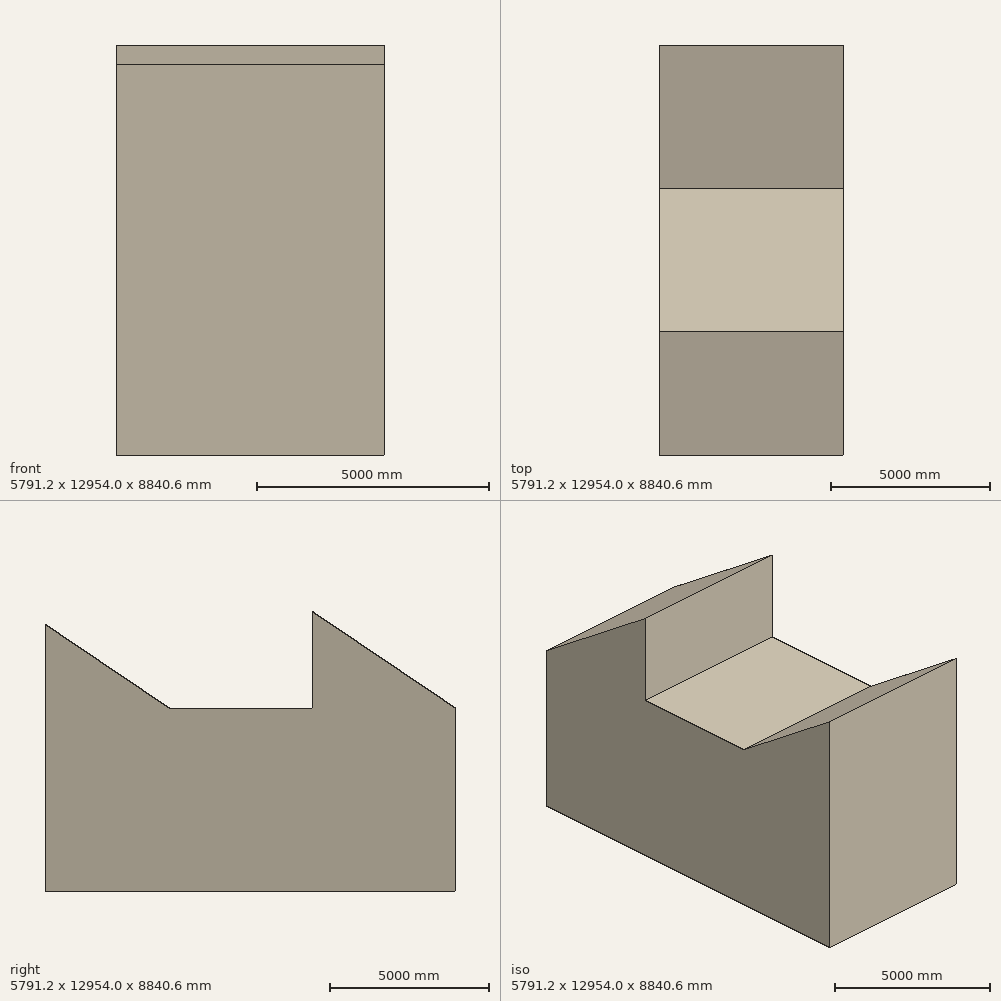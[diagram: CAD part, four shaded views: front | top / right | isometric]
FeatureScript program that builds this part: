
annotation { "Feature Type Name" : "Feature", "Feature Type Description" : "" }
export const myFeature = defineFeature(function(context is Context, id is Id, definition is map)
    precondition{}
    {
        {
            var Q0;
            Q0=qCreatedBy(makeId("Right.planeOp"),FACE);
            var sketch = newSketch(context, id + "F0", { "sketchPlane" : qUnion([Q0])});
            skLineSegment(sketch, "E0.bottom", {"start": v(-3648.98, 2419.57) * mm, "end": v(9305.02, 2419.57) * mm});
            skLineSegment(sketch, "E0.top", {"start": v(-3648.98, -3371.63) * mm, "end": v(9305.02, -3371.63) * mm});
            skLineSegment(sketch, "E0.left", {"start": v(-3648.98, 2419.57) * mm, "end": v(-3648.98, -3371.63) * mm});
            skLineSegment(sketch, "E0.right", {"start": v(9305.02, 2419.57) * mm, "end": v(9305.02, -3371.63) * mm});
            skLineSegment(sketch, "E1", {"start": v(-3648.98, 5058.27) * mm, "end": v(263.06, 2419.57) * mm});
            skLineSegment(sketch, "E2", {"start": v(4784.04, 5469.01) * mm, "end": v(9305.02, 2419.57) * mm});
            skLineSegment(sketch, "E3", {"start": v(4784.04, 5469.01) * mm, "end": v(263.06, 2419.57) * mm, "construction": true});
            skLineSegment(sketch, "E4", {"start": v(4784.04, 5469.01) * mm, "end": v(4784.04, 2419.57) * mm});
            skLineSegment(sketch, "E5", {"start": v(-3648.98, 5058.27) * mm, "end": v(-3648.98, 2419.57) * mm});
            skSolve(sketch);
        }
        {
            var Q0;
            Q0 = qSketchRegion(id + "F0", true);
            extrude(context, id + "F1", {"entities" : qUnion([Q0]), "endBound" : BoundingType.SYMMETRIC, "depth" : 5791.2 * mm});
        }
    });
